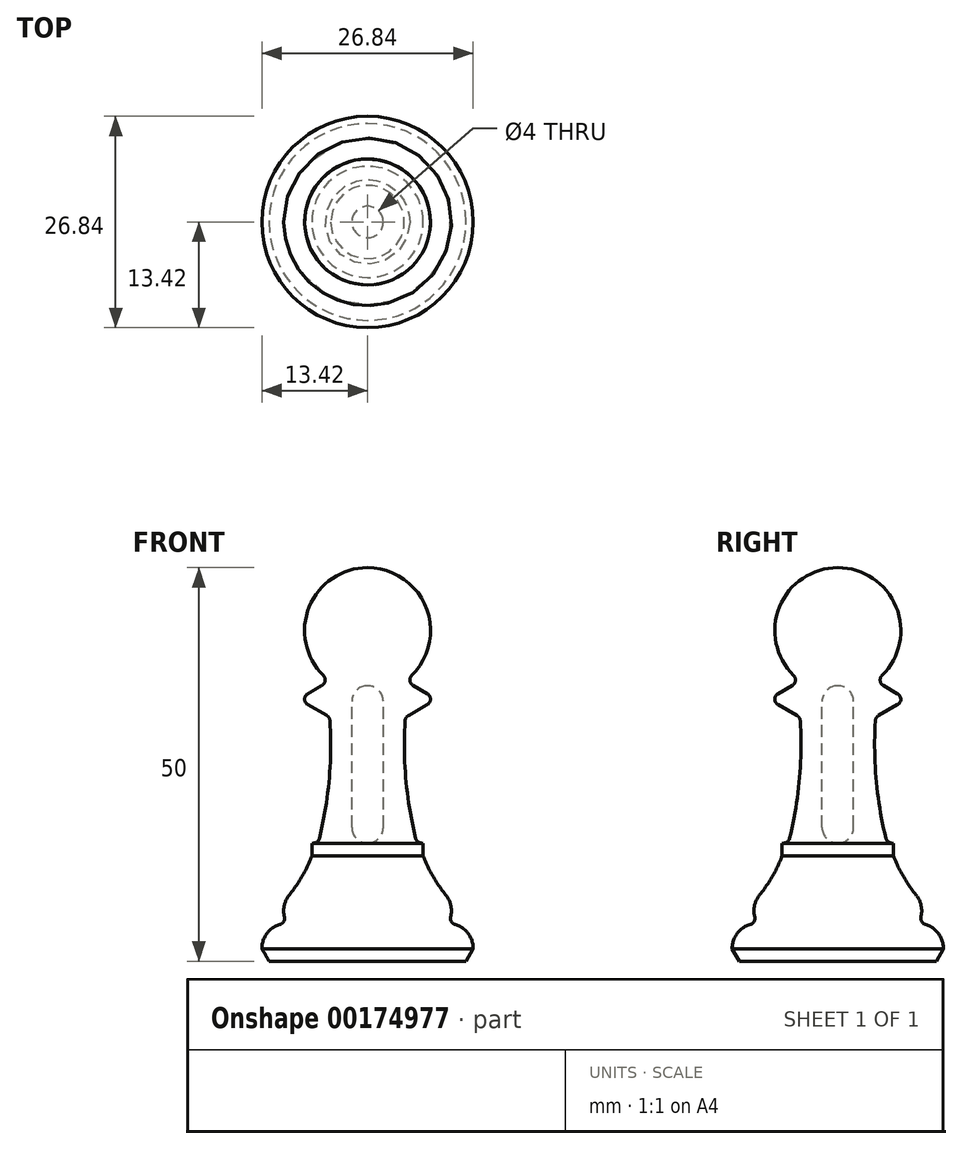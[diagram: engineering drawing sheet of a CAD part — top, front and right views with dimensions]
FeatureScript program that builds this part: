
annotation { "Feature Type Name" : "Feature", "Feature Type Description" : "" }
export const myFeature = defineFeature(function(context is Context, id is Id, definition is map)
    precondition{}
    {
        {
            var Q0;
            Q0=qCreatedBy(makeId("Front.planeOp"),FACE);
            var sketch = newSketch(context, id + "F0", { "sketchPlane" : qUnion([Q0])});
            skLineSegment(sketch, "E0", {"start": v(0, 0) * mm, "end": v(12.5, 0) * mm});
            skLineSegment(sketch, "E1", {"start": v(0, 0) * mm, "end": v(0, 95) * mm, "construction": true});
            skLineSegment(sketch, "E2", {"start": v(0, 15) * mm, "end": v(7.07, 15) * mm, "construction": true});
            skLineSegment(sketch, "E3", {"start": v(12.7, 32) * mm, "end": v(0, 32) * mm, "construction": true});
            skLineSegment(sketch, "E4", {"start": v(0, 46.8) * mm, "end": v(12.7, 46.8) * mm, "construction": true});
            skLineSegment(sketch, "E5", {"start": v(12.5, 0) * mm, "end": v(13.42, 1.6) * mm});
            skArc(sketch, "E6", {"start": v(13.42, 1.6) * mm, "mid": v(12.49, 3.86) * mm, "end": v(10.22, 4.8) * mm});
            skLineSegment(sketch, "E7", {"start": v(7.07, 15) * mm, "end": v(7.07, 13.4) * mm});
            skArc(sketch, "E8", {"start": v(7.07, 13.4) * mm, "mid": v(8.3, 10.8) * mm, "end": v(9.94, 8.42) * mm});
            skArc(sketch, "E9", {"start": v(10.22, 4.8) * mm, "mid": v(10.64, 6.65) * mm, "end": v(9.94, 8.42) * mm});
            skLineSegment(sketch, "E10", {"start": v(7.07, 15) * mm, "end": v(6.27, 15) * mm});
            skLineSegment(sketch, "E11", {"start": v(0, 50) * mm, "end": v(0, 0) * mm});
            skArc(sketch, "E12", {"start": v(0, 50) * mm, "mid": v(7.59, 44.53) * mm, "end": v(4.8, 35.6) * mm});
            skLineSegment(sketch, "E13", {"start": v(4.8, 35.6) * mm, "end": v(8.8, 33.3) * mm});
            skLineSegment(sketch, "E14", {"start": v(4.8, 30.98) * mm, "end": v(8.8, 33.3) * mm});
            skArc(sketch, "E15", {"start": v(4.8, 30.98) * mm, "mid": v(4.89, 22.93) * mm, "end": v(6.27, 15) * mm});
            skSolve(sketch);
        }
        {
            var Q0;
            Q0=qSketchRegion(id+"F0",true);
            var Q1;
            Q1=sQuery(id+"F0.wireOp",EDGE,"E1");
            revolve(context, id + "F1", {"entities" : qUnion([Q0]), "axis" : qUnion([Q1]), "revolveType" : RevolveType.FULL});
        }
        {
            var Q0;
            Q0=qCreatedBy(makeId("Front.planeOp"),FACE);
            var sketch = newSketch(context, id + "F2", { "sketchPlane" : qUnion([Q0])});
            skLineSegment(sketch, "E16.bottom", {"start": v(0, 15) * mm, "end": v(0, 15) * mm});
            skLineSegment(sketch, "E16.top", {"start": v(0.5, 35) * mm, "end": v(0, 35) * mm});
            skLineSegment(sketch, "E16.left", {"start": v(2, 17) * mm, "end": v(2, 33) * mm});
            skPoint(sketch, "E16.middle", {"position": v(0, 25) * mm});
            skPoint(sketch, "E17.visualSharp", {"position": v(2, 35) * mm});
            skArc(sketch, "E17.filletArc", {"start": v(2, 33) * mm, "mid": v(1.41, 34.41) * mm, "end": v(0, 35) * mm});
            skPoint(sketch, "E18.visualSharp", {"position": v(-2, 35) * mm});
            skPoint(sketch, "E19.visualSharp", {"position": v(-2, 15) * mm});
            skPoint(sketch, "E20.visualSharp", {"position": v(2, 15) * mm});
            skArc(sketch, "E20.filletArc", {"start": v(0, 15) * mm, "mid": v(1.41, 15.59) * mm, "end": v(2, 17) * mm});
            skLineSegment(sketch, "E21", {"start": v(0, 35) * mm, "end": v(0, 15) * mm});
            skSolve(sketch);
        }
        {
            var Q0;
            Q0=qSketchRegion(id+"F2",true);
            var Q1;
            Q1=qConstructionFilter(qBodyType(qCreatedBy(id+"F2",EDGE),BodyType.WIRE),ConstructionObject.NO);
            var Q2;
            Q2=sQuery(id+"F2.wireOp",EDGE,"E21");
            revolve(context, id + "F3", {"operationType" : NewBodyOperationType.REMOVE, "entities" : qUnion([Q0]), "surfaceEntities" : qUnion([Q1]), "axis" : qUnion([Q2]), "revolveType" : RevolveType.FULL});
        }
        {
            var Q0;
            Q0=makeQuery(id+"F1.opRevolve","SWEPT_EDGE",EDGE,{"disambiguationData":[OSD([sQuery(id+"F0.wireOp",EDGE,"E13"),sQuery(id+"F0.wireOp",EDGE,"E14")])]});
            var Q1;
            Q1=makeQuery(id+"F1.opRevolve","SWEPT_EDGE",EDGE,{"disambiguationData":[OSD([sQuery(id+"F0.wireOp",EDGE,"E14"),sQuery(id+"F0.wireOp",EDGE,"E15")])]});
            var Q2;
            Q2=makeQuery(id+"F1.opRevolve","SWEPT_EDGE",EDGE,{"disambiguationData":[OSD([sQuery(id+"F0.wireOp",EDGE,"E12"),sQuery(id+"F0.wireOp",EDGE,"E13")])]});
            var Q3;
            Q3=makeQuery(id+"F1.opRevolve","SWEPT_EDGE",EDGE,{"disambiguationData":[OSD([sQuery(id+"F0.wireOp",EDGE,"E10"),sQuery(id+"F0.wireOp",EDGE,"E15")])]});
            var Q4;
            Q4=makeQuery(id+"F1.opRevolve","SWEPT_EDGE",EDGE,{"disambiguationData":[OSD([sQuery(id+"F0.wireOp",EDGE,"E6"),sQuery(id+"F0.wireOp",EDGE,"E9")])]});
            fillet(context, id + "F4", {"entities" : qUnion([Q0, Q1, Q2, Q3, Q4]), "radius" : .8 * mm, "tangentPropagation" : true, "allowEdgeOverflow" : false});
        }
    });
